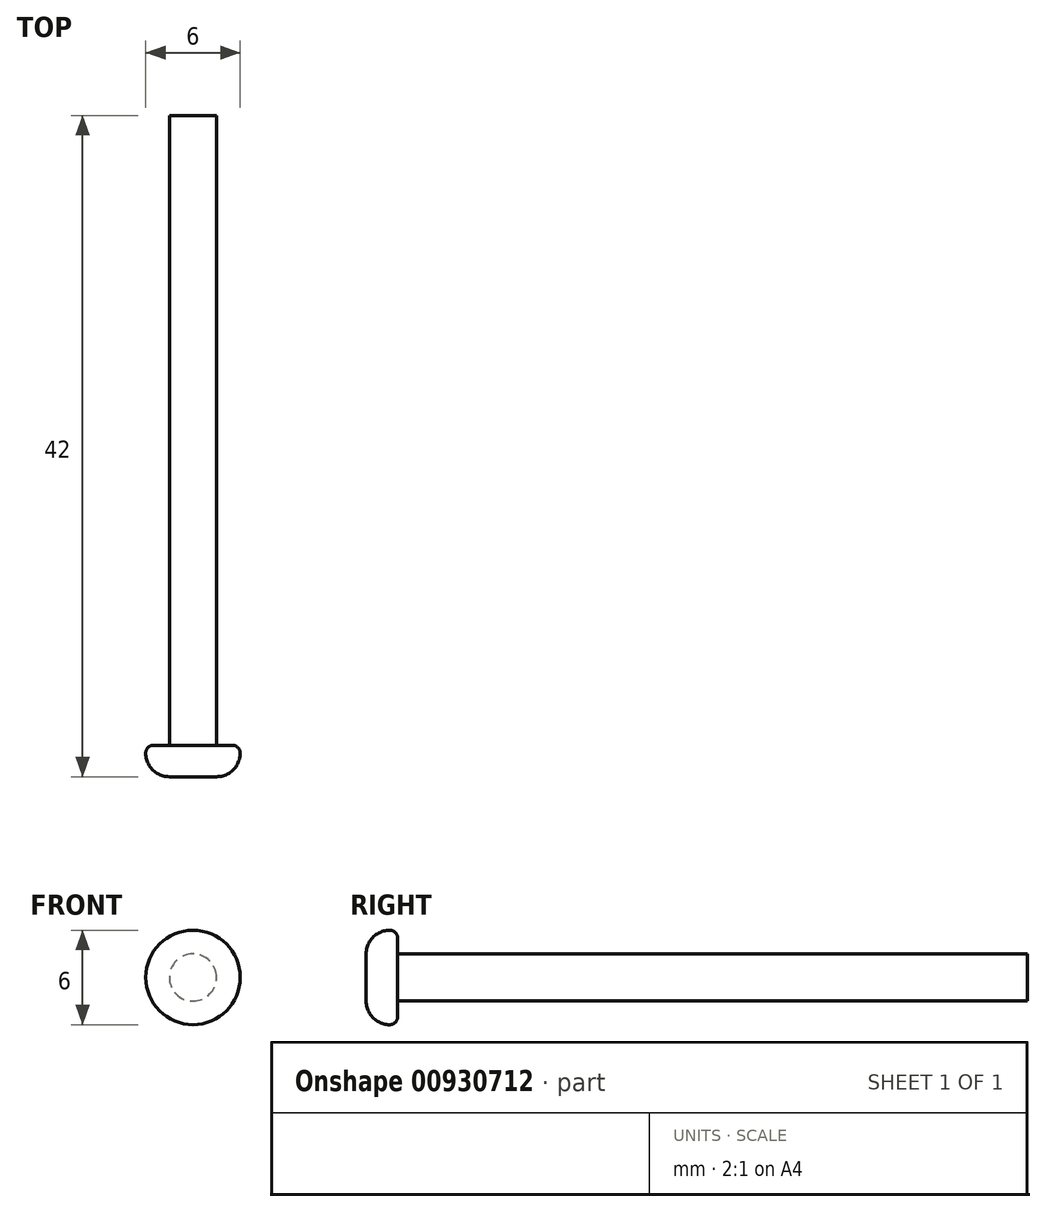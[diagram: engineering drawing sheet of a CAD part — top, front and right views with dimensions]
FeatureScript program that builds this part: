
annotation { "Feature Type Name" : "Feature", "Feature Type Description" : "" }
export const myFeature = defineFeature(function(context is Context, id is Id, definition is map)
    precondition{}
    {
        {
            var Q0;
            Q0=qCreatedBy(makeId("Front.planeOp"),FACE);
            var sketch = newSketch(context, id + "F0", { "sketchPlane" : qUnion([Q0])});
            skCircle(sketch, "E0", {"center": v(0, 0) * mm, "radius": 1.5 * mm});
            skSolve(sketch);
        }
        {
            var Q0;
            Q0=makeQuery(id+"F0.imprint","IMPRINT",FACE,{"disambiguationData":[TD([[makeQuery(id+"F0.imprint","IMPRINT",EDGE,{"derivedFrom":sQuery(id+"F0.wireOp",EDGE,"E0")}),1.0]])]});
            var Q1;
            Q1=sQuery(id+"F0.wireOp",EDGE,"E0");
            extrude(context, id + "F1", {"entities" : qUnion([Q0]), "surfaceEntities" : qUnion([Q1]), "oppositeDirection" : true, "depth" : 40 * mm, "offsetDistance" : 25 * mm});
        }
        {
            var Q0;
            Q0=makeQuery(id+"F1.opExtrude","CAP_FACE",FACE,{"disambiguationData":[OSD([sQuery(id+"F0.wireOp",EDGE,"E0")])],"isStart":true});
            var sketch = newSketch(context, id + "F2", { "sketchPlane" : qUnion([Q0])});
            skCircle(sketch, "E1", {"center": v(0, 0) * mm, "radius": 3 * mm});
            skSolve(sketch);
        }
        {
            var Q0;
            Q0 = qSketchRegion(id + "F2", true);
            extrude(context, id + "F3", {"entities" : qUnion([Q0]), "operationType" : NewBodyOperationType.ADD, "depth" : 2 * mm, "offsetDistance" : 25 * mm});
        }
        {
            var Q0;
            Q0=makeQuery(id+"F3.opExtrude","CAP_EDGE",EDGE,{"disambiguationData":[OSD([sQuery(id+"F2.wireOp",EDGE,"E1")])],"isStart":false});
            fillet(context, id + "F4", {"entities" : qUnion([Q0]), "radius" : 1.5 * mm, "tangentPropagation" : true, "allowEdgeOverflow" : false});
        }
        {
            var Q0;
            Q0=makeQuery(id+"F3.opExtrude","CAP_EDGE",EDGE,{"disambiguationData":[OSD([sQuery(id+"F2.wireOp",EDGE,"E1")])],"isStart":true});
            fillet(context, id + "F5", {"entities" : qUnion([Q0]), "radius" : 0.5 * mm, "tangentPropagation" : true, "allowEdgeOverflow" : false});
        }
    });
